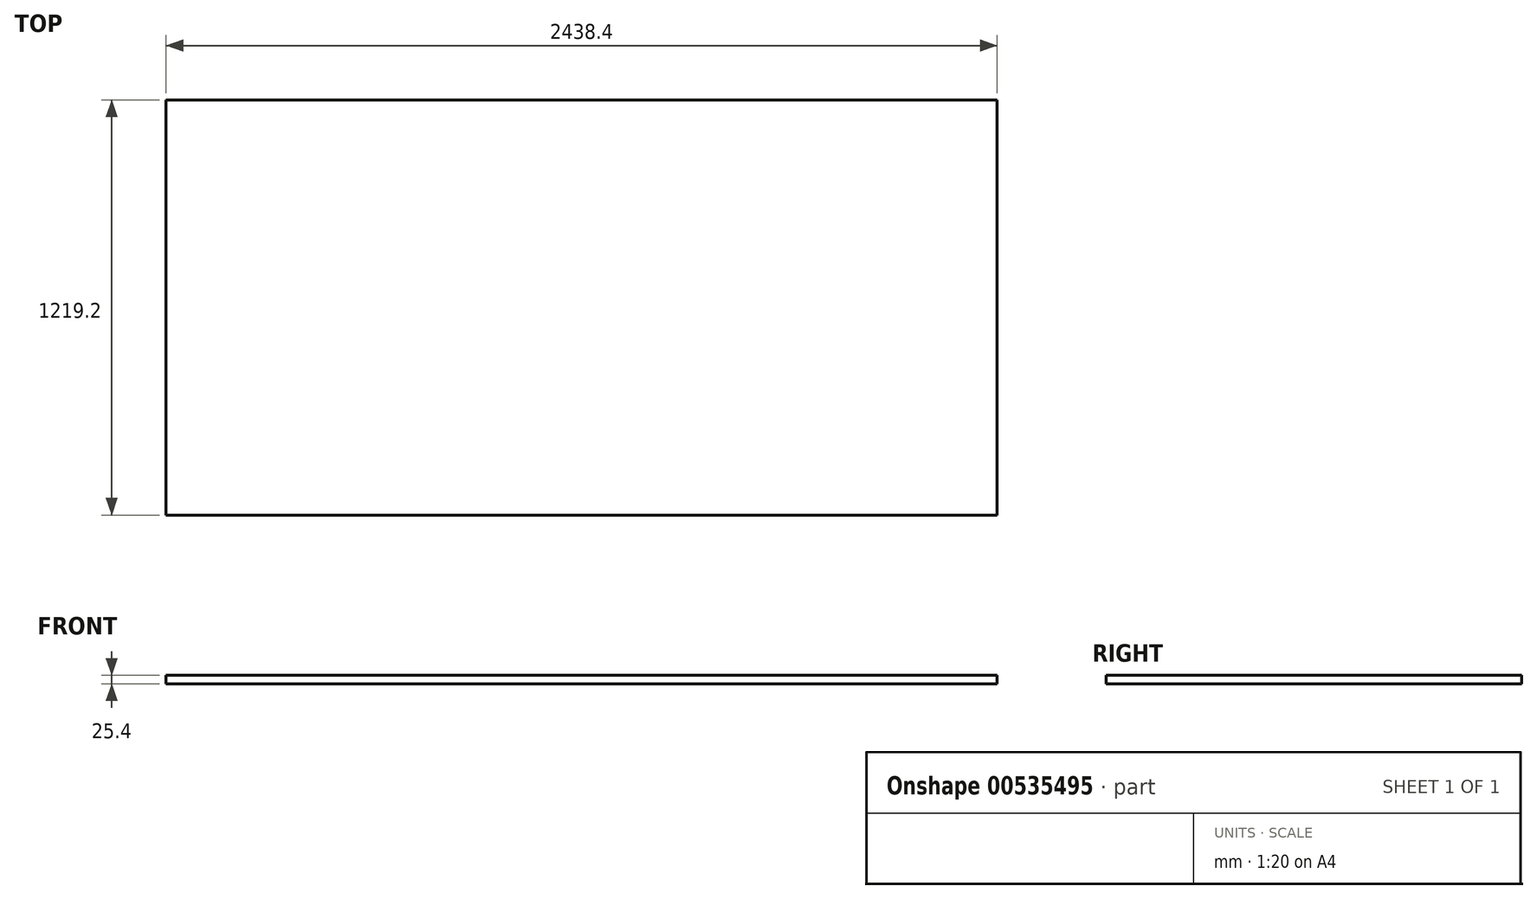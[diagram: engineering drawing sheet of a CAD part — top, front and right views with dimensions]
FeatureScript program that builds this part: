
annotation { "Feature Type Name" : "Feature", "Feature Type Description" : "" }
export const myFeature = defineFeature(function(context is Context, id is Id, definition is map)
    precondition{}
    {
        {
            var Q0;
            Q0=qCreatedBy(makeId("Top.planeOp"),FACE);
            var sketch = newSketch(context, id + "F0", { "sketchPlane" : qUnion([Q0])});
            skLineSegment(sketch, "E0.bottom", {"start": v(-93.5, 1175.1) * mm, "end": v(2344.9, 1175.1) * mm});
            skLineSegment(sketch, "E0.top", {"start": v(-93.5, -44.1) * mm, "end": v(2344.9, -44.1) * mm});
            skLineSegment(sketch, "E0.left", {"start": v(-93.5, 1175.1) * mm, "end": v(-93.5, -44.1) * mm});
            skLineSegment(sketch, "E0.right", {"start": v(2344.9, 1175.1) * mm, "end": v(2344.9, -44.1) * mm});
            skSolve(sketch);
        }
        {
            var Q0;
            Q0=makeQuery(id+"F0.imprint","IMPRINT",FACE,{"disambiguationData":[TD([[makeQuery(id+"F0.imprint","IMPRINT",EDGE,{"derivedFrom":sQuery(id+"F0.wireOp",EDGE,"E0.bottom")}),-1.0]])]});
            extrude(context, id + "F1", {"entities" : qUnion([Q0]), "depth" : 25.4 * mm, "offsetDistance" : 25.4 * mm});
        }
    });
